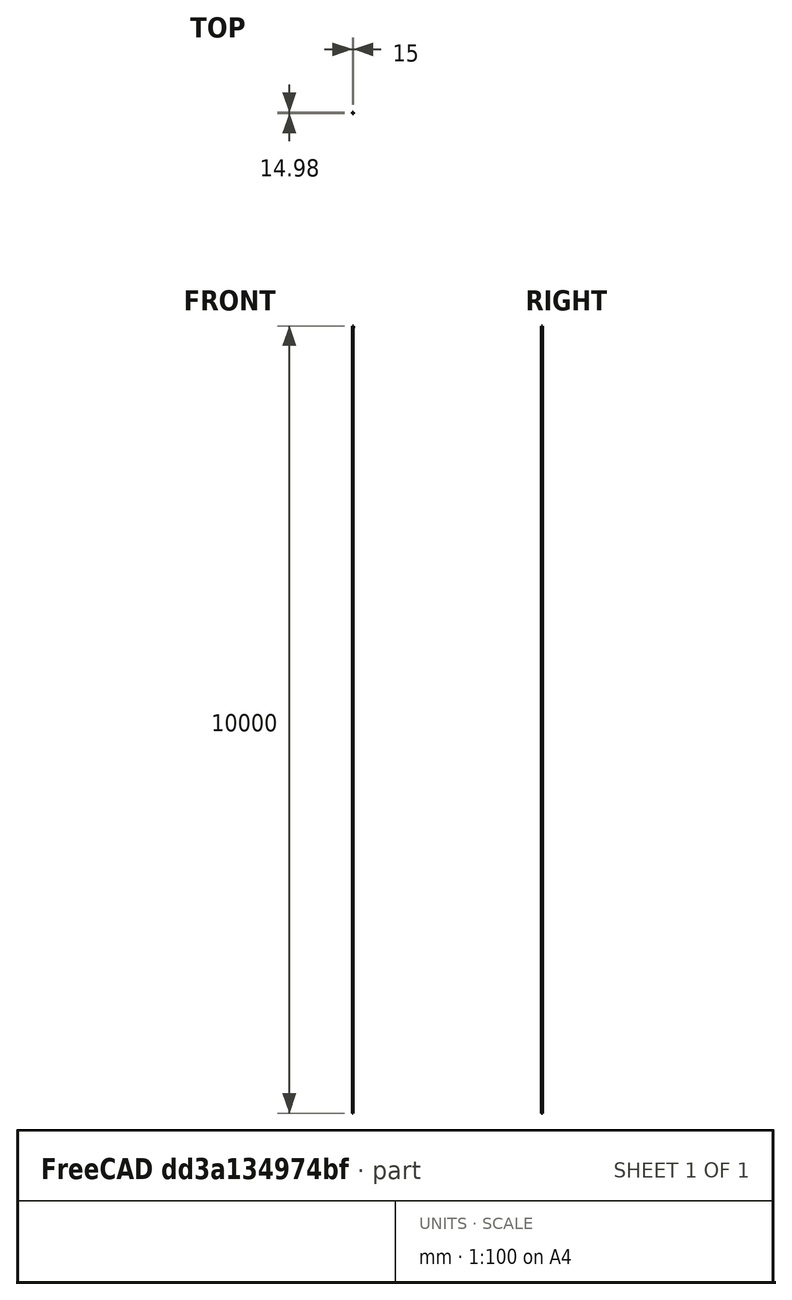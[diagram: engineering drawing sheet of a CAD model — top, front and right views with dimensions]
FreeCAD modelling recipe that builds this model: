
FCSTD DOCUMENT  (FreeCAD 0.15R4671 (Git))
Label: IGUS_8mm_Bearing
License: All rights reserved
LicenseURL: http://en.wikipedia.org/wiki/All_rights_reserved
objects: Part::Feature×3, Mesh::Feature×2, Sketcher::SketchObject×1, PartDesign::Pocket×1
note: 6 computed .brp shape members not serialized (recipe doc carries the construction recipe); baked Part::Feature solids carry a one-line shape summary decoded from their .brp

FEATURE [Part::Feature] Part__Feature  label="LM8UU_0_5_Nozzle_V3001"
  shape: bbox 15 x 15 x 24 mm, 476 faces, 0 solids (baked)
FEATURE [Mesh::Feature] BUSHING
FEATURE [Mesh::Feature] Printed_8mm_IGUS_bushing
FEATURE [Part::Feature] Printed_8mm_IGUS_bushing001
  shape: bbox 15 x 14.99 x 24 mm, 4632 faces, 0 solids (baked)
FEATURE [Part::Feature] Printed_8mm_IGUS_bushing001_solid  label="Printed_8mm_IGUS_bushing001 (Solid)"
  shape: bbox 15 x 14.99 x 24 mm, 4632 faces (baked)
FEATURE [Sketcher::SketchObject] Sketch
  Placement = pos=(0,0,24) rot=(0,0,1;0rad)
  Support = -> Printed_8mm_IGUS_bushing001_solid [Face4584]
  sketch-geometry (1):
    g0: Circle CenterX=0 CenterY=0 CenterZ=0 NormalX=0 NormalY=0 NormalZ=1 Radius=4.25
  constraints (1):
    c: Radius(g0) = 4.25
FEATURE [PartDesign::Pocket] Pocket
  Length = 5
  Sketch = -> Sketch
  Type = 1
